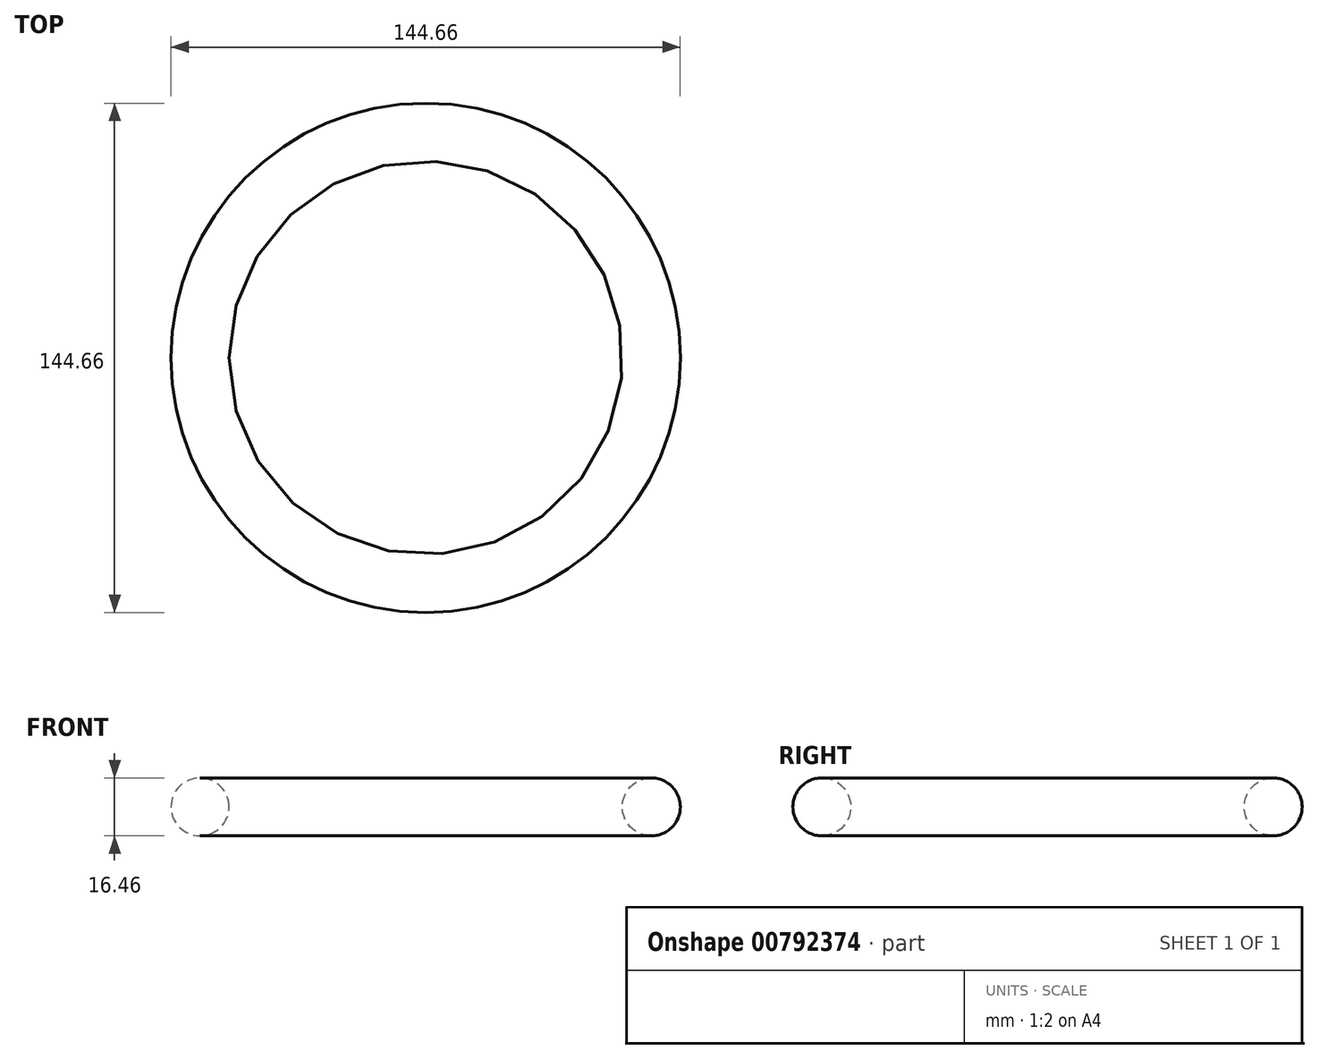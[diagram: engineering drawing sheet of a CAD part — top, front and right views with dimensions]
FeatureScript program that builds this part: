
annotation { "Feature Type Name" : "Feature", "Feature Type Description" : "" }
export const myFeature = defineFeature(function(context is Context, id is Id, definition is map)
    precondition{}
    {
        {
            var Q0;
            Q0=qCreatedBy(makeId("Top.planeOp"),FACE);
            var sketch = newSketch(context, id + "F0", { "sketchPlane" : qUnion([Q0])});
            skCircle(sketch, "E0", {"center": v(0, 0) * mm, "radius": 64.1 * mm});
            skSolve(sketch);
        }
        {
            var Q0;
            Q0=qCreatedBy(makeId("Front.planeOp"),FACE);
            var sketch = newSketch(context, id + "F1", { "sketchPlane" : qUnion([Q0])});
            skCircle(sketch, "E1", {"center": v(64.1, 0) * mm, "radius": 8.23 * mm});
            skSolve(sketch);
        }
        {
            var Q0;
            Q0 = qSketchRegion(id + "F1", true);
            var Q1;
            Q1=sQuery(id+"F0.wireOp",EDGE,"E0");
            revolve(context, id + "F2", {"surfaceOperationType" : NewSurfaceOperationType.NEW, "entities" : qUnion([Q0]), "axis" : qUnion([Q1]), "revolveType" : RevolveType.FULL});
        }
    });
